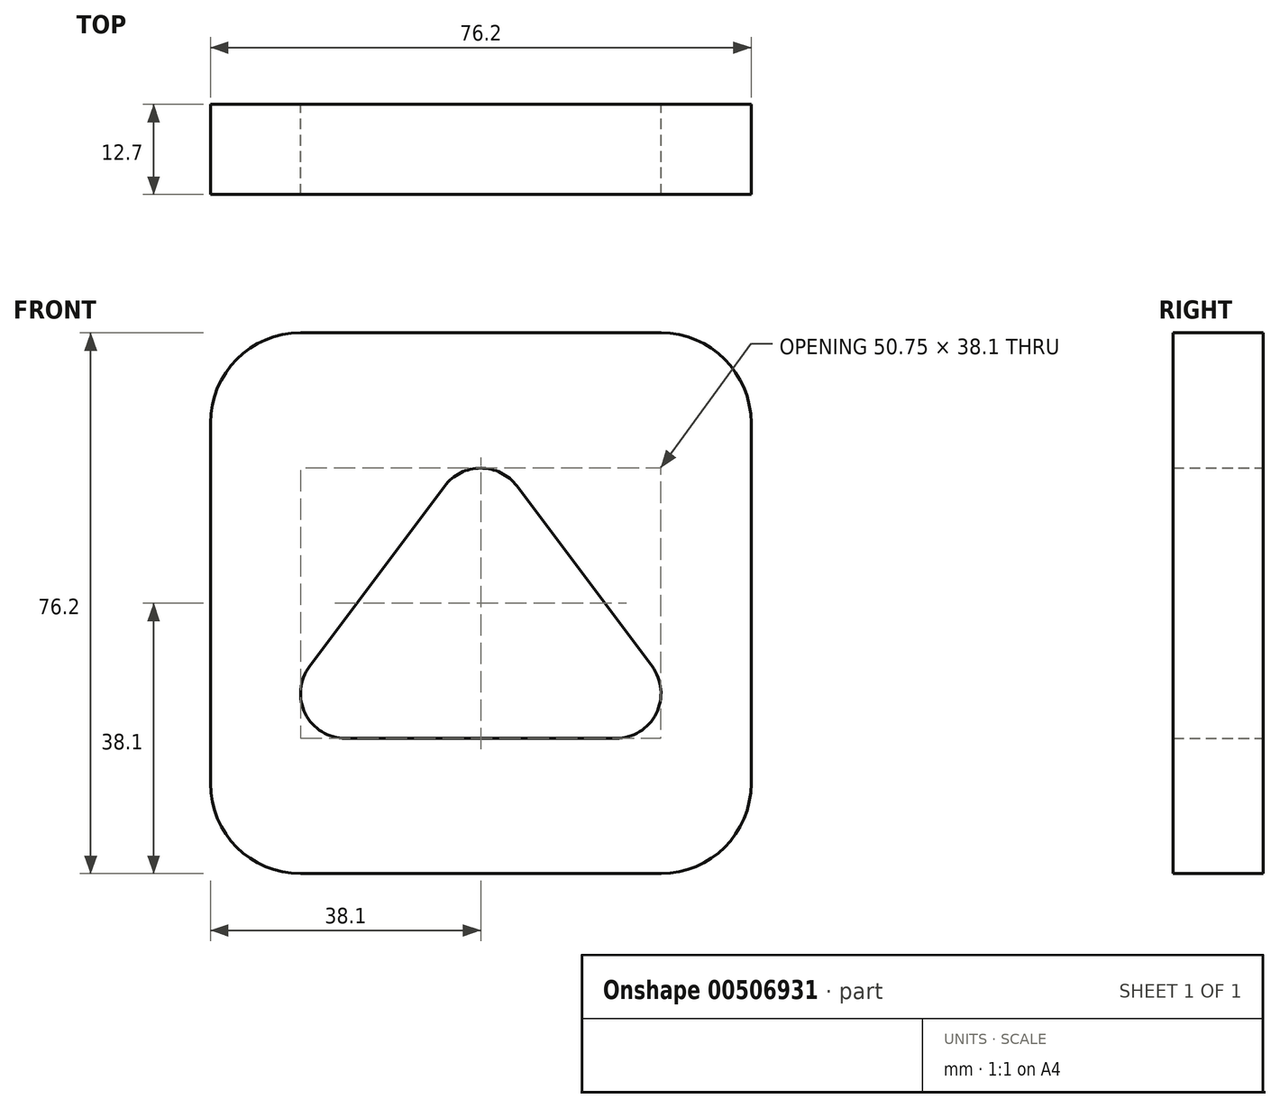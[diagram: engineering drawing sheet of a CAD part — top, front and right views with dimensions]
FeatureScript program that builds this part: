
annotation { "Feature Type Name" : "Feature", "Feature Type Description" : "" }
export const myFeature = defineFeature(function(context is Context, id is Id, definition is map)
    precondition{}
    {
        {
            var Q0;
            Q0=qCreatedBy(makeId("Front.planeOp"),FACE);
            var sketch = newSketch(context, id + "F0", { "sketchPlane" : qUnion([Q0])});
            skLineSegment(sketch, "E0", {"start": v(76.2, 12.7) * mm, "end": v(76.2, 63.5) * mm});
            skLineSegment(sketch, "E1", {"start": v(63.5, 76.2) * mm, "end": v(12.7, 76.2) * mm});
            skLineSegment(sketch, "E2", {"start": v(0, 63.5) * mm, "end": v(0, 12.7) * mm});
            skLineSegment(sketch, "E3", {"start": v(12.7, 0) * mm, "end": v(63.5, 0) * mm});
            skArc(sketch, "E4", {"start": v(13.97, 29.21) * mm, "mid": v(13.37, 22.56) * mm, "end": v(19.05, 19.05) * mm});
            skArc(sketch, "E5", {"start": v(57.15, 19.05) * mm, "mid": v(62.83, 22.56) * mm, "end": v(62.23, 29.21) * mm});
            skArc(sketch, "E6", {"start": v(43.18, 54.6) * mm, "mid": v(38.1, 57.15) * mm, "end": v(33.02, 54.6) * mm});
            skLineSegment(sketch, "E7", {"start": v(33.02, 54.6) * mm, "end": v(13.97, 29.21) * mm});
            skLineSegment(sketch, "E8", {"start": v(19.05, 19.05) * mm, "end": v(57.15, 19.05) * mm});
            skLineSegment(sketch, "E9", {"start": v(62.23, 29.21) * mm, "end": v(43.18, 54.6) * mm});
            skArc(sketch, "E10", {"start": v(12.7, 76.2) * mm, "mid": v(3.72, 72.48) * mm, "end": v(0, 63.5) * mm});
            skPoint(sketch, "E11.orphan", {"position": v(0, 76.2) * mm});
            skArc(sketch, "E12", {"start": v(76.2, 63.5) * mm, "mid": v(72.48, 72.48) * mm, "end": v(63.5, 76.2) * mm});
            skArc(sketch, "E13", {"start": v(0, 12.7) * mm, "mid": v(3.72, 3.72) * mm, "end": v(12.7, 0) * mm});
            skArc(sketch, "E14", {"start": v(63.5, 0) * mm, "mid": v(72.48, 3.72) * mm, "end": v(76.2, 12.7) * mm});
            skSolve(sketch);
        }
        {
            var Q0;
            Q0=makeQuery(id+"F0.imprint","IMPRINT",FACE,{"disambiguationData":[TD([[makeQuery(id+"F0.imprint","IMPRINT",EDGE,{"derivedFrom":sQuery(id+"F0.wireOp",EDGE,"E0")}),1.0]])]});
            extrude(context, id + "F1", {"entities" : qUnion([Q0]), "depth" : 12.7 * mm});
        }
    });
